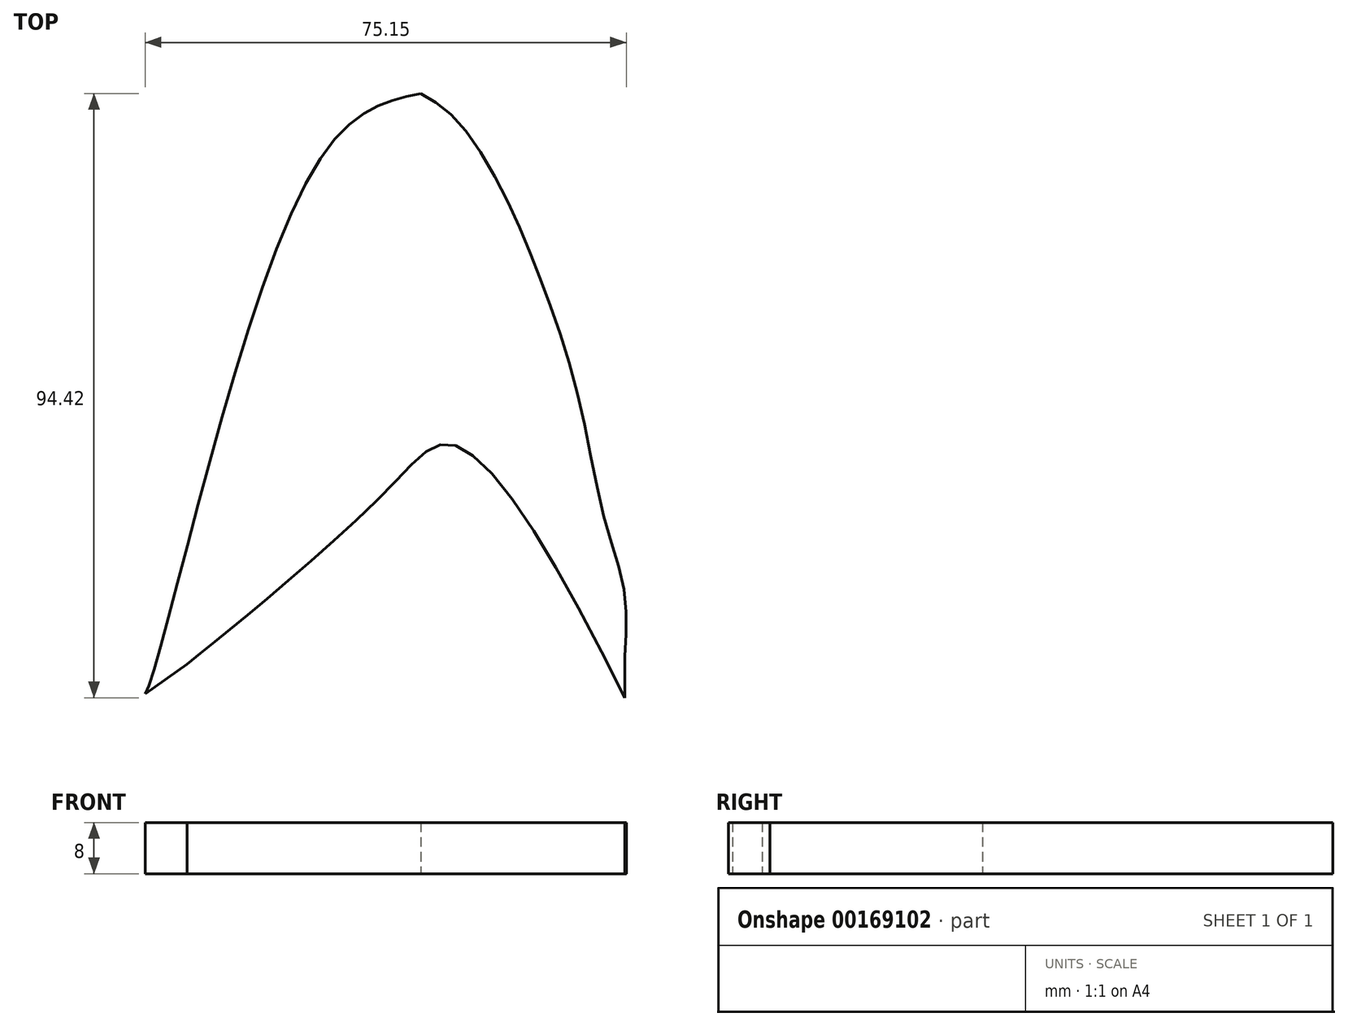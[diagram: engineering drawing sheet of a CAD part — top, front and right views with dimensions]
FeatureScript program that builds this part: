
annotation { "Feature Type Name" : "Feature", "Feature Type Description" : "" }
export const myFeature = defineFeature(function(context is Context, id is Id, definition is map)
    precondition{}
    {
        {
            var Q0;
            Q0=qCreatedBy(makeId("Top.planeOp"),FACE);
            var sketch = newSketch(context, id + "F0", { "sketchPlane" : qUnion([Q0])});
            skFitSpline(sketch, "E0", {"points": [v(0, 46.93) * mm, v(-17.33, 34.13) * mm, v(-43.07, -46.9) * mm, v(-43.32, -47.14) * mm], "startDerivative": vector(-52.98, -11.17) * mm, "endDerivative": vector(1.18, -2.93) * mm});
            skLineSegment(sketch, "E1", {"start": v(-43.07, -46.9) * mm, "end": v(-36.55, -42.27) * mm});
            skFitSpline(sketch, "E2", {"points": [v(-36.55, -42.27) * mm, v(-25.93, -33.58) * mm, v(-4.65, -14.42) * mm, v(4.9, -7.93) * mm, v(31.82, -47.5) * mm], "startDerivative": vector(48.39, 38.52) * mm, "endDerivative": vector(81.98, -166.47) * mm});
            skLineSegment(sketch, "E3", {"start": v(31.82, -47.5) * mm, "end": v(31.82, -41.04) * mm});
            skFitSpline(sketch, "E4", {"points": [v(31.82, -41.04) * mm, v(31.82, -31.2) * mm, v(28.58, -19.14) * mm, v(24.47, 0) * mm, v(19, 16.97) * mm, v(13, 31.22) * mm, v(5.48, 42.86) * mm, v(0, 46.93) * mm], "startDerivative": vector(4.5, 80) * mm, "endDerivative": vector(-54.2, 31.57) * mm});
            skSolve(sketch);
        }
        {
            var Q0;
            {var subQ0=sQuery(id+"F0.wireOp",EDGE,"E1");Q0=makeQuery(id+"F0.imprint","IMPRINT",FACE,{"disambiguationData":[TD([[makeQuery(id+"F0.imprint","IMPRINT",EDGE,{"derivedFrom":subQ0}),1.0]])]});}
            extrude(context, id + "F1", {"entities" : qUnion([Q0]), "depth" : 8 * mm});
        }
    });
